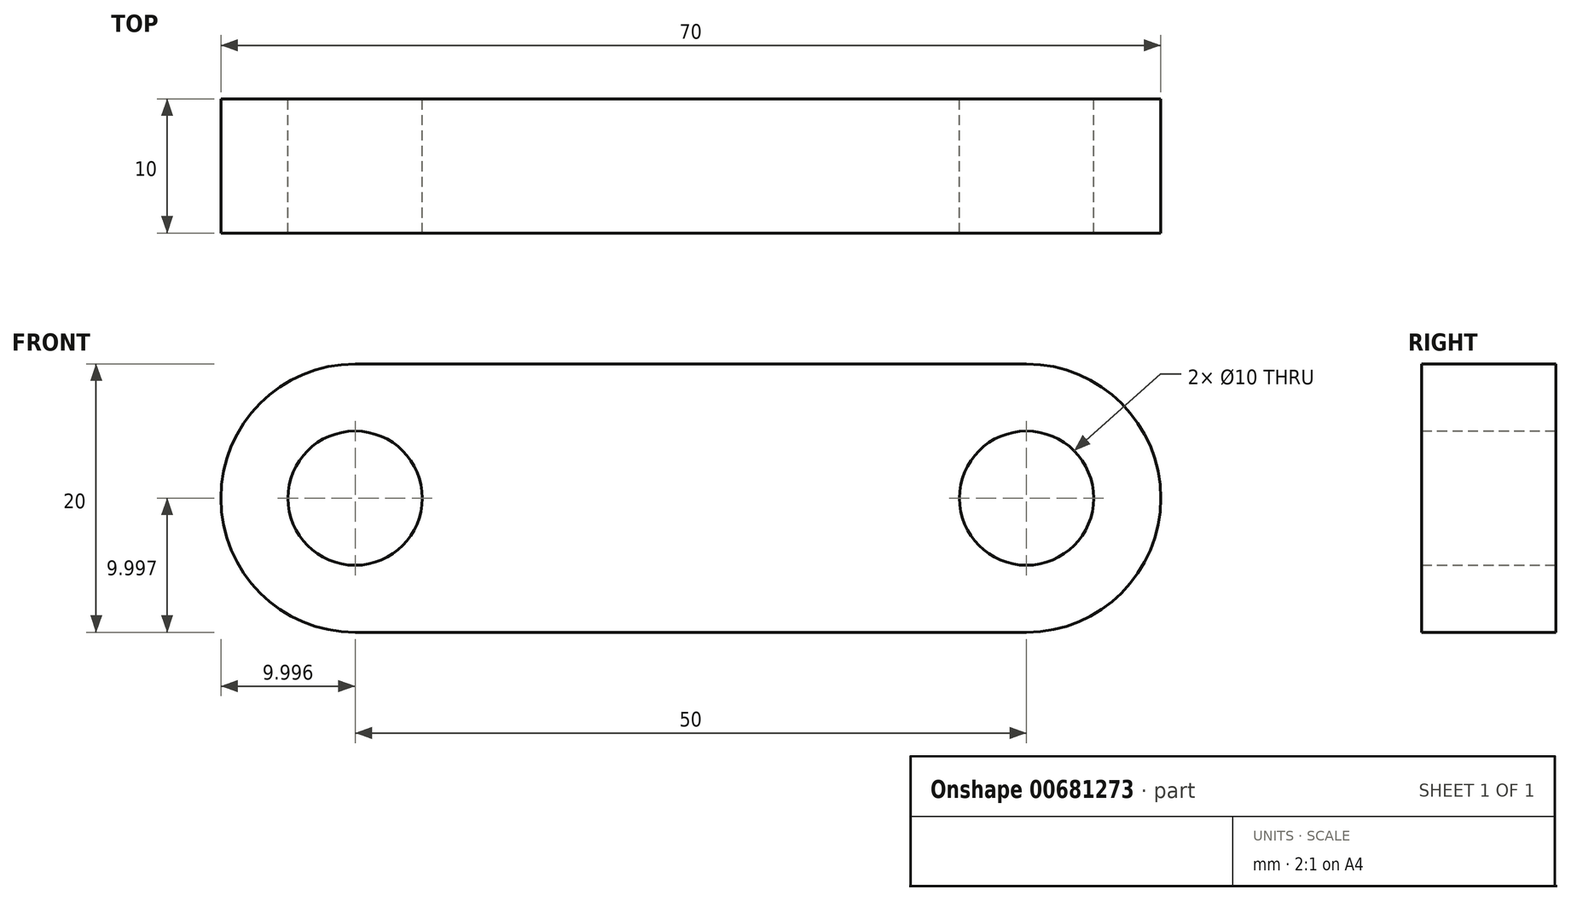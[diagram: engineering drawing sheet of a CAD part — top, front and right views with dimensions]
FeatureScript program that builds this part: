
annotation { "Feature Type Name" : "Feature", "Feature Type Description" : "" }
export const myFeature = defineFeature(function(context is Context, id is Id, definition is map)
    precondition{}
    {
        {
            var Q0;
            Q0=qCreatedBy(makeId("Front.planeOp"),FACE);
            var sketch = newSketch(context, id + "F0", { "sketchPlane" : qUnion([Q0])});
            skLineSegment(sketch, "E0.bottom", {"start": v(-37.93, 9.33) * mm, "end": v(12.07, 9.33) * mm});
            skLineSegment(sketch, "E0.top", {"start": v(-37.93, -10.67) * mm, "end": v(12.07, -10.67) * mm});
            skArc(sketch, "E1", {"start": v(-37.93, -10.67) * mm, "mid": v(-47.93, -0.67) * mm, "end": v(-37.93, 9.33) * mm});
            skPoint(sketch, "E2.endSnap0", {"position": v(-12.93, 9.33) * mm});
            skArc(sketch, "E3", {"start": v(12.07, -10.67) * mm, "mid": v(22.07, -0.67) * mm, "end": v(12.07, 9.33) * mm});
            skCircle(sketch, "E4", {"center": v(-37.93, -0.67) * mm, "radius": 5 * mm});
            skCircle(sketch, "E5", {"center": v(12.07, -0.67) * mm, "radius": 5 * mm});
            skSolve(sketch);
        }
        {
            var Q0;
            Q0=makeQuery(id+"F0.imprint","IMPRINT",FACE,{"disambiguationData":[TD([[makeQuery(id+"F0.imprint","IMPRINT",EDGE,{"derivedFrom":sQuery(id+"F0.wireOp",EDGE,"E0.bottom")}),-1.0]])]});
            extrude(context, id + "F1", {"entities" : qUnion([Q0]), "depth" : 10 * mm, "offsetDistance" : 25 * mm});
        }
    });
